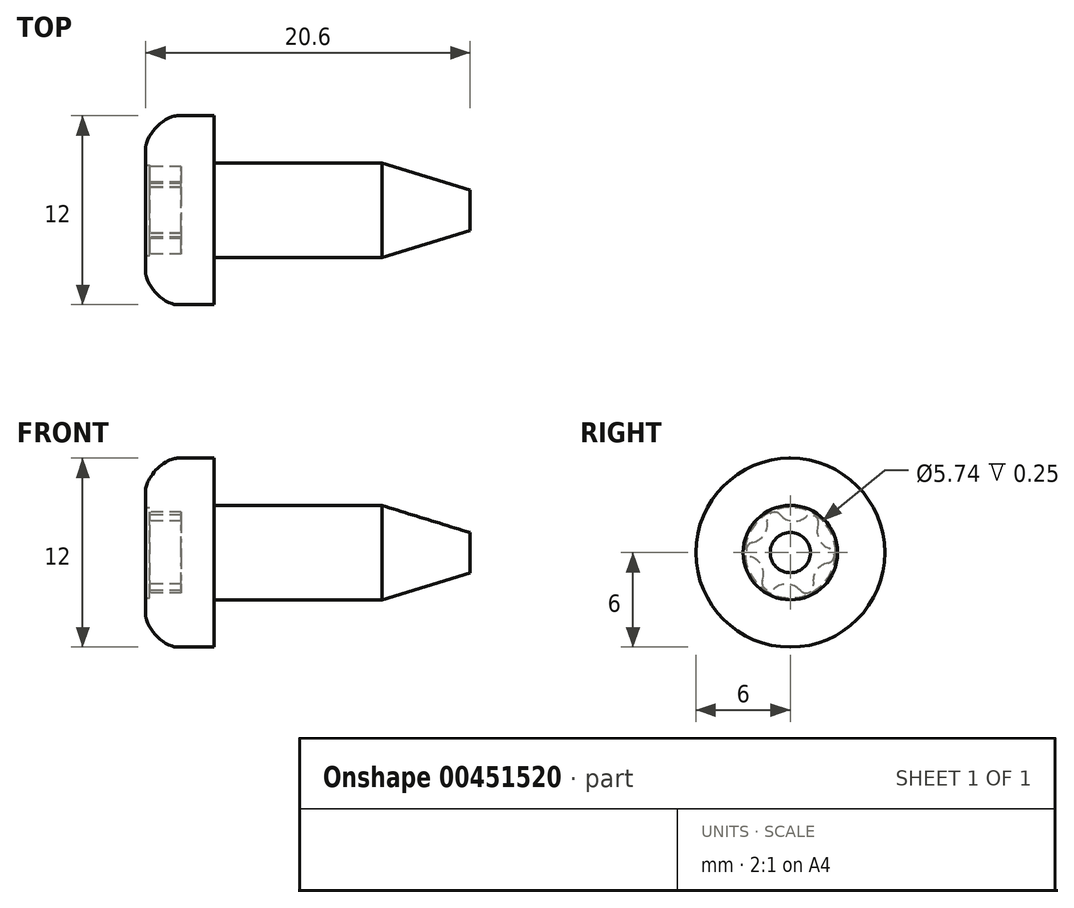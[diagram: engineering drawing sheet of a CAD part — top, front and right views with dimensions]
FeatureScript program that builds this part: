
annotation { "Feature Type Name" : "Feature", "Feature Type Description" : "" }
export const myFeature = defineFeature(function(context is Context, id is Id, definition is map)
    precondition{}
    {
        {
            var Q0;
            Q0=qCreatedBy(makeId("Top.planeOp"),FACE);
            var sketch = newSketch(context, id + "F0", { "sketchPlane" : qUnion([Q0])});
            skLineSegment(sketch, "E0", {"start": v(0, 0) * mm, "end": v(20.6, 0) * mm});
            skLineSegment(sketch, "E1", {"start": v(0, 0) * mm, "end": v(0, -6) * mm});
            skLineSegment(sketch, "E2", {"start": v(0, -6) * mm, "end": v(4.35, -6) * mm});
            skLineSegment(sketch, "E3", {"start": v(4.35, -6) * mm, "end": v(4.35, -3) * mm});
            skLineSegment(sketch, "E4", {"start": v(4.35, -3) * mm, "end": v(15, -3) * mm});
            skLineSegment(sketch, "E5", {"start": v(15, -3) * mm, "end": v(20.6, -1.27) * mm});
            skLineSegment(sketch, "E6", {"start": v(20.6, 0) * mm, "end": v(20.6, -1.27) * mm});
            skSolve(sketch);
        }
        {
            var Q0;
            Q0=qSketchRegion(id+"F0",true);
            var Q1;
            Q1=sQuery(id+"F0.wireOp",EDGE,"E0");
            revolve(context, id + "F1", {"entities" : qUnion([Q0]), "axis" : qUnion([Q1]), "revolveType" : RevolveType.FULL});
        }
        {
            var Q0;
            Q0=qCreatedBy(makeId("Top.planeOp"),FACE);
            var sketch = newSketch(context, id + "F2", { "sketchPlane" : qUnion([Q0])});
            skLineSegment(sketch, "E7", {"start": v(0, 0) * mm, "end": v(0.25, 0) * mm});
            skLineSegment(sketch, "E8", {"start": v(0.25, 0) * mm, "end": v(0.25, 2.87) * mm});
            skLineSegment(sketch, "E9", {"start": v(0.25, 2.87) * mm, "end": v(0, 2.87) * mm});
            skLineSegment(sketch, "E10", {"start": v(0, 2.87) * mm, "end": v(0, 0) * mm});
            skSolve(sketch);
        }
        {
            var Q0;
            Q0=qSketchRegion(id+"F2",true);
            var Q1;
            Q1=sQuery(id+"F2.wireOp",EDGE,"E7");
            revolve(context, id + "F3", {"operationType" : NewBodyOperationType.REMOVE, "entities" : qUnion([Q0]), "axis" : qUnion([Q1]), "revolveType" : RevolveType.FULL, "oppositeDirection" : true});
        }
        {
            var Q0;
            Q0=makeQuery(id+"F1.opRevolve","SWEPT_FACE",FACE,{"disambiguationData":[OSD([sQuery(id+"F0.wireOp",EDGE,"E1")])]});
            var sketch = newSketch(context, id + "F4", { "sketchPlane" : qUnion([Q0])});
            skArc(sketch, "E11.4.0", {"start": v(2.47, -0.27) * mm, "mid": v(1.82, -0.87) * mm, "end": v(1.77, -1.75) * mm});
            skPoint(sketch, "E11.center", {"position": v(0, 0) * mm});
            skArc(sketch, "E12.1.0", {"start": v(1.47, 2) * mm, "mid": v(1.66, 1.14) * mm, "end": v(2.4, 0.65) * mm});
            skArc(sketch, "E12.2.0", {"start": v(-1, 2.28) * mm, "mid": v(-0.16, 2) * mm, "end": v(0.63, 2.4) * mm});
            skArc(sketch, "E12.3.0", {"start": v(-2.47, 0.27) * mm, "mid": v(-1.82, 0.87) * mm, "end": v(-1.77, 1.75) * mm});
            skArc(sketch, "E12.4.0", {"start": v(-1.47, -2) * mm, "mid": v(-1.66, -1.14) * mm, "end": v(-2.4, -0.65) * mm});
            skArc(sketch, "E12.5.0", {"start": v(1, -2.28) * mm, "mid": v(0.16, -2) * mm, "end": v(-0.63, -2.4) * mm});
            skArc(sketch, "E13", {"start": v(2.47, -0.27) * mm, "mid": v(2.79, 0.22) * mm, "end": v(2.4, 0.65) * mm});
            skArc(sketch, "E14.1.0", {"start": v(1.47, 2) * mm, "mid": v(1.2, 2.53) * mm, "end": v(0.63, 2.4) * mm});
            skArc(sketch, "E14.2.0", {"start": v(-1, 2.28) * mm, "mid": v(-1.58, 2.3) * mm, "end": v(-1.77, 1.75) * mm});
            skArc(sketch, "E14.3.0", {"start": v(-2.47, 0.27) * mm, "mid": v(-2.79, -0.22) * mm, "end": v(-2.4, -0.65) * mm});
            skArc(sketch, "E14.4.0", {"start": v(-1.47, -2) * mm, "mid": v(-1.2, -2.53) * mm, "end": v(-0.63, -2.4) * mm});
            skArc(sketch, "E14.5.0", {"start": v(1, -2.28) * mm, "mid": v(1.58, -2.3) * mm, "end": v(1.77, -1.75) * mm});
            skSolve(sketch);
        }
        {
            var Q0;
            Q0=qSketchRegion(id+"F4",true);
            extrude(context, id + "F5", {"entities" : qUnion([Q0]), "operationType" : NewBodyOperationType.REMOVE, "oppositeDirection" : true, "depth" : 2.25 * mm});
        }
        {
            var Q0;
            Q0=makeQuery(id+"F1.opRevolve","SWEPT_EDGE",EDGE,{"disambiguationData":[OSD([sQuery(id+"F0.wireOp",EDGE,"E1"),sQuery(id+"F0.wireOp",EDGE,"E2")])]});
            fillet(context, id + "F6", {"entities" : qUnion([Q0]), "radius" : 2 * mm, "tangentPropagation" : true, "rho" : 0.3, "crossSection" : FilletCrossSection.CONIC, "allowEdgeOverflow" : false});
        }
    });
